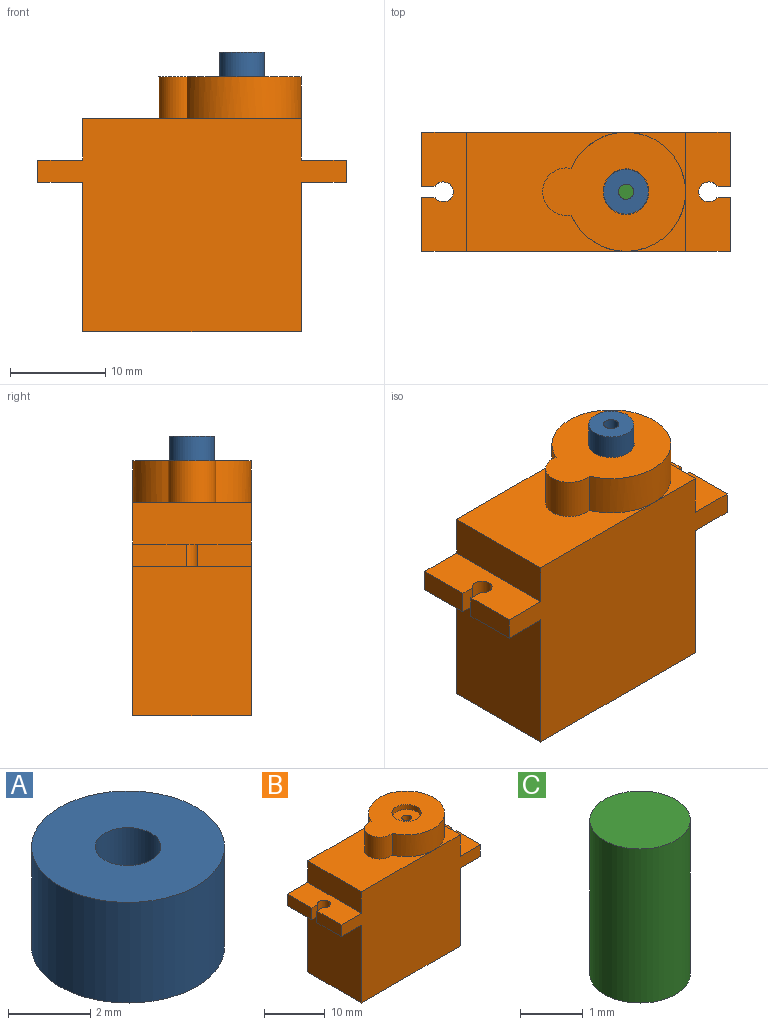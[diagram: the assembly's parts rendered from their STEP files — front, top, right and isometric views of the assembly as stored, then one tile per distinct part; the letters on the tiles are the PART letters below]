
ASSEMBLY  parts=3 mates=2
PART A: 4 faces, bbox 4.7x4.7x3 mm
  f0: cylinder r=0.8mm len=3mm, axis (0,0,-1), area 15.1mm2, adj f2,f3
  f1: cylinder r=2.35mm len=4.7mm, axis (0,0,-1), area 44.3mm2, adj f2,f3
  f2: plane 4.7x4.7mm, normal (0,0,1), area 15.3mm2, adj f0,f1
  f3: plane 4.7x4.7mm, normal (0,0,-1), area 15.3mm2, adj f0,f1
PART B: 31 faces, bbox 32.4x12.5x26.8 mm
  f0: plane 16.75x12.5mm, normal (0,0,1), area 137.4mm2, adj f15,f16,f17,f24,f25
  f1: plane 6.25x6.25mm, normal (0,0,1), area 8.4mm2, adj f13,f16,f24
  f2: plane 5.65x2.36mm, normal (-1,0,0), area 13.3mm2, adj f4,f6,f16,f22
  f3: plane 5.65x2.36mm, normal (1,0,0), area 13.3mm2, adj f5,f11,f16,f20
  f4: plane 12.5x4.7mm, normal (0,0,-1), area 53.8mm2, adj f2,f7,f8,f16,f17,f21,f22,f23
  f5: plane 12.5x4.7mm, normal (0,0,1), area 53.8mm2, adj f3,f12,f13,f16,f17,f18,f19,f20
  f6: plane 12.5x4.7mm, normal (0,0,1), area 53.8mm2, adj f2,f7,f15,f16,f17,f21,f22,f23
  f7: plane 5.65x2.36mm, normal (-1,0,0), area 13.3mm2, adj f4,f6,f17,f23
  f8: plane 15.7x12.5mm, normal (-1,0,0), area 196.2mm2, adj f4,f9,f16,f17
  f9: plane 23x12.5mm, normal (0,0,-1), area 287.5mm2, adj f8,f10,f16,f17
  f10: plane 15.7x12.5mm, normal (1,0,0), area 196.2mm2, adj f9,f11,f16,f17
  f11: plane 12.5x4.7mm, normal (0,0,-1), area 53.8mm2, adj f3,f10,f12,f16,f17,f18,f19,f20
  f12: plane 5.65x2.36mm, normal (1,0,0), area 13.3mm2, adj f5,f11,f17,f18
  f13: plane 12.5x4.34mm, normal (1,0,0), area 54.3mm2, adj f1,f5,f14,f16,f17
  f14: plane 6.25x6.25mm, normal (0,0,1), area 8.4mm2, adj f13,f17,f24
  f15: plane 12.5x4.34mm, normal (-1,0,0), area 54.3mm2, adj f0,f6,f16,f17
  f16: plane 32.4x22.4mm, normal (0,-1,0), area 537.4mm2, adj f0,f1,f2,f3,f4,f5,f6,f8
  f17: plane 32.4x22.4mm, normal (0,1,0), area 537.4mm2, adj f0,f4,f5,f6,f7,f8,f9,f10
  f18: plane 2.36x1.39mm, normal (0,-1,0), area 3.3mm2, adj f5,f11,f12,f19
  f19: cylinder r=1.05mm len=2.36mm, axis (0,0,1), area 12.6mm2, adj f5,f11,f18,f20
  f20: plane 2.36x1.39mm, normal (0,1,0), area 3.3mm2, adj f3,f5,f11,f19
  f21: cylinder r=1.05mm len=2.36mm, axis (0,0,1), area 12.6mm2, adj f4,f6,f22,f23
  f22: plane 2.36x1.39mm, normal (0,1,0), area 3.3mm2, adj f2,f4,f6,f21
  f23: plane 2.36x1.39mm, normal (0,-1,0), area 3.3mm2, adj f4,f6,f7,f21
  f24: cylinder r=6.25mm len=12.5mm, axis (0,0,-1), area 150.6mm2, adj f0,f1,f14,f25,f26
  f25: cylinder r=2.5mm len=5mm, axis (0,0,-1), area 39mm2, adj f0,f24,f26
  f26: plane 15x12.5mm, normal (0,0,1), area 115.3mm2, adj f24,f25,f27
  f27: cylinder r=2.4mm len=4.8mm, axis (0,0,1), area 15.1mm2, adj f26,f28
  f28: plane 4.8x4.8mm, normal (0,0,1), area 16.1mm2, adj f27,f29
  f29: cylinder r=0.8mm len=1.6mm, axis (0,0,1), area 5mm2, adj f28,f30
  f30: plane 1.6x1.6mm, normal (0,0,1), area 2mm2, adj f29
PART C: 3 faces, bbox 1.6x1.6x3 mm
  f0: cylinder r=0.8mm len=3mm, axis (0,0,-1), area 15.1mm2, adj f1,f2
  f1: plane 1.6x1.6mm, normal (0,0,1), area 2mm2, adj f0
  f2: plane 1.6x1.6mm, normal (0,0,-1), area 2mm2, adj f0
PLACE A t=(5.25,0,26.4)mm
PLACE B t=(-11.5,6.25,0)mm
PLACE C t=(5.25,0,24.8)mm
MATE fastened C.f0 <-> B.f24  axis (0,0,-1) through (5.25,0,24.8)mm
MATE fastened A.f1 <-> C.f0  axis (0,0,1) through (5.25,0,29.4)mm
